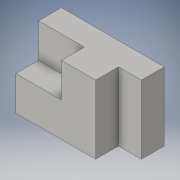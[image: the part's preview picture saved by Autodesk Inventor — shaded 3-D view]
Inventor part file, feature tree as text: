
AUTODESK INVENTOR PART (.ipt)
format: ipt  version: 2016 (Build 200138000, 138)  size: 108,032 bytes
history: native  units: in
note: dims shown in document units (in); Inventor stores cm internally (conversion verified against a paired STEP export)
features: extrude x3, sketch x3
ambient origin geometry x8: Origin, YZ Plane, XZ Plane, XY Plane, X Axis, Y Axis, Z Axis, Center Point
bodies: Solid1 (feature_tree)
feature tree (6):
  extrude  "Extrusion1"  Depth=1.5in
  extrude  "Extrusion2"  Depth=0.75in
  extrude  "Extrusion3"  Depth=0.5in TaperAngle=0.0deg
  sketch  "Sketch1"  dims[d0=2.25in d1=1.5in]
  sketch  "Sketch2"  dims[d2=1.0in d3=0.0in d4=0.75in]
  sketch  "Sketch3"  dims[d5=1.0in d6=0.5in d7=0.0in d8=0.5in d9=0.5in d10=0.0in]
